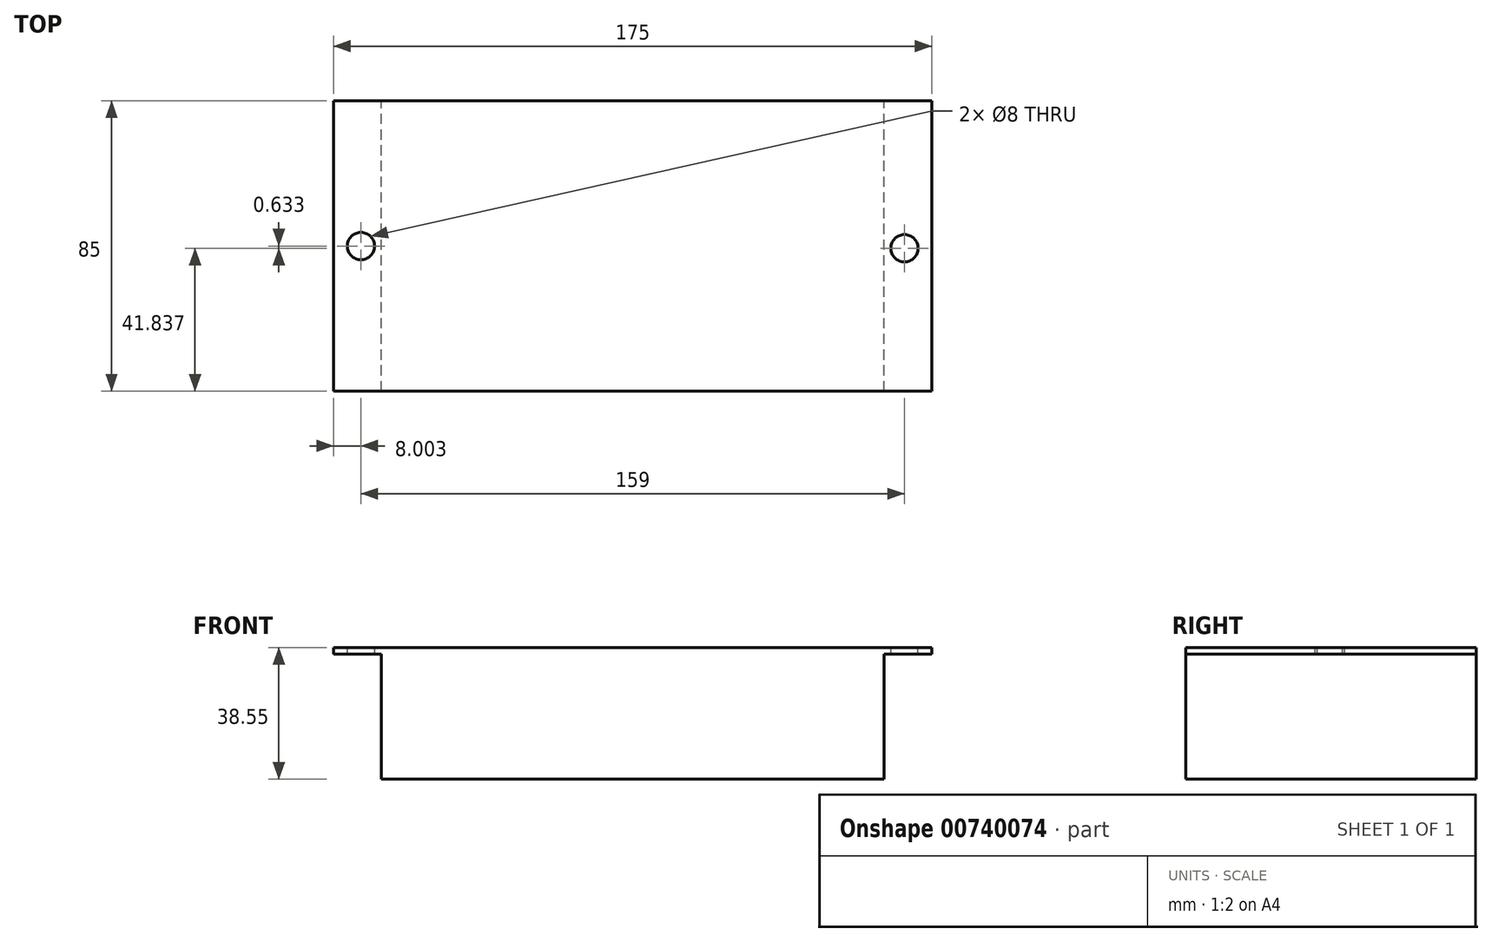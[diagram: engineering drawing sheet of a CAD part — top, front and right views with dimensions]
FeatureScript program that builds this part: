
annotation { "Feature Type Name" : "Feature", "Feature Type Description" : "" }
export const myFeature = defineFeature(function(context is Context, id is Id, definition is map)
    precondition{}
    {
        {
            var Q0;
            Q0=qCreatedBy(makeId("Front.planeOp"),FACE);
            var sketch = newSketch(context, id + "F0", { "sketchPlane" : qUnion([Q0])});
            skLineSegment(sketch, "E0.bottom", {"start": v(-79.39, -11.3) * mm, "end": v(67.61, -11.3) * mm});
            skLineSegment(sketch, "E0.top", {"start": v(-79.39, -49.86) * mm, "end": v(67.61, -49.86) * mm});
            skLineSegment(sketch, "E0.left", {"start": v(-79.39, -13.3) * mm, "end": v(-79.39, -49.86) * mm});
            skLineSegment(sketch, "E0.right", {"start": v(67.61, -13.3) * mm, "end": v(67.61, -49.86) * mm});
            skLineSegment(sketch, "E1.bottom", {"start": v(67.61, -11.3) * mm, "end": v(81.61, -11.3) * mm});
            skLineSegment(sketch, "E1.top", {"start": v(67.61, -13.3) * mm, "end": v(81.61, -13.3) * mm});
            skLineSegment(sketch, "E1.right", {"start": v(81.61, -11.3) * mm, "end": v(81.61, -13.3) * mm});
            skLineSegment(sketch, "E2.bottom", {"start": v(-79.39, -11.3) * mm, "end": v(-93.39, -11.3) * mm});
            skLineSegment(sketch, "E2.top", {"start": v(-79.39, -13.3) * mm, "end": v(-93.39, -13.3) * mm});
            skLineSegment(sketch, "E2.right", {"start": v(-93.39, -11.3) * mm, "end": v(-93.39, -13.3) * mm});
            skSolve(sketch);
        }
        {
            var Q0;
            Q0 = qSketchRegion(id + "F0", true);
            extrude(context, id + "F1", {"entities" : qUnion([Q0]), "depth" : 85 * mm, "offsetDistance" : 25 * mm});
        }
        {
            var Q0;
            Q0=makeQuery(id+"F1.opExtrude","SWEPT_FACE",FACE,{"disambiguationData":[OSD([sQuery(id+"F0.wireOp",EDGE,"E0.bottom"),sQuery(id+"F0.wireOp",EDGE,"E1.bottom"),sQuery(id+"F0.wireOp",EDGE,"E2.bottom")])]});
            var sketch = newSketch(context, id + "F2", { "sketchPlane" : qUnion([Q0])});
            skLineSegment(sketch, "E3", {"start": v(-85.39, -5.21) * mm, "end": v(-85.39, -77.44) * mm, "construction": true});
            skLineSegment(sketch, "E4", {"start": v(73.61, -7.1) * mm, "end": v(73.61, -79.23) * mm, "construction": true});
            skLineSegment(sketch, "E5", {"start": v(-93.39, -42.5) * mm, "end": v(81.61, -43.16) * mm, "construction": true});
            skPoint(sketch, "E5.endSnap0", {"position": v(81.61, -42.5) * mm});
            skPoint(sketch, "E5.endSnap1", {"position": v(73.61, -43.16) * mm});
            skCircle(sketch, "E6", {"center": v(-85.39, -42.53) * mm, "radius": 4 * mm});
            skCircle(sketch, "E7", {"center": v(73.61, -43.16) * mm, "radius": 4 * mm});
            skSolve(sketch);
        }
        {
            var Q0;
            Q0=makeQuery(id+"F2.imprint","IMPRINT",FACE,{"disambiguationData":[TD([[makeQuery(id+"F2.imprint","IMPRINT",EDGE,{"derivedFrom":sQuery(id+"F2.wireOp",EDGE,"E6")}),1.0]])]});
            var Q1;
            Q1=makeQuery(id+"F2.imprint","IMPRINT",FACE,{"disambiguationData":[TD([[makeQuery(id+"F2.imprint","IMPRINT",EDGE,{"derivedFrom":sQuery(id+"F2.wireOp",EDGE,"E7")}),1.0]])]});
            var Q2;
            Q2=sQuery(id+"F2.wireOp",EDGE,"E6");
            var Q3;
            Q3=sQuery(id+"F2.wireOp",EDGE,"E7");
            extrude(context, id + "F3", {"entities" : qUnion([Q0, Q1]), "operationType" : NewBodyOperationType.REMOVE, "surfaceEntities" : qUnion([Q2, Q3]), "oppositeDirection" : true, "depth" : 25 * mm, "offsetDistance" : 25 * mm});
        }
    });
